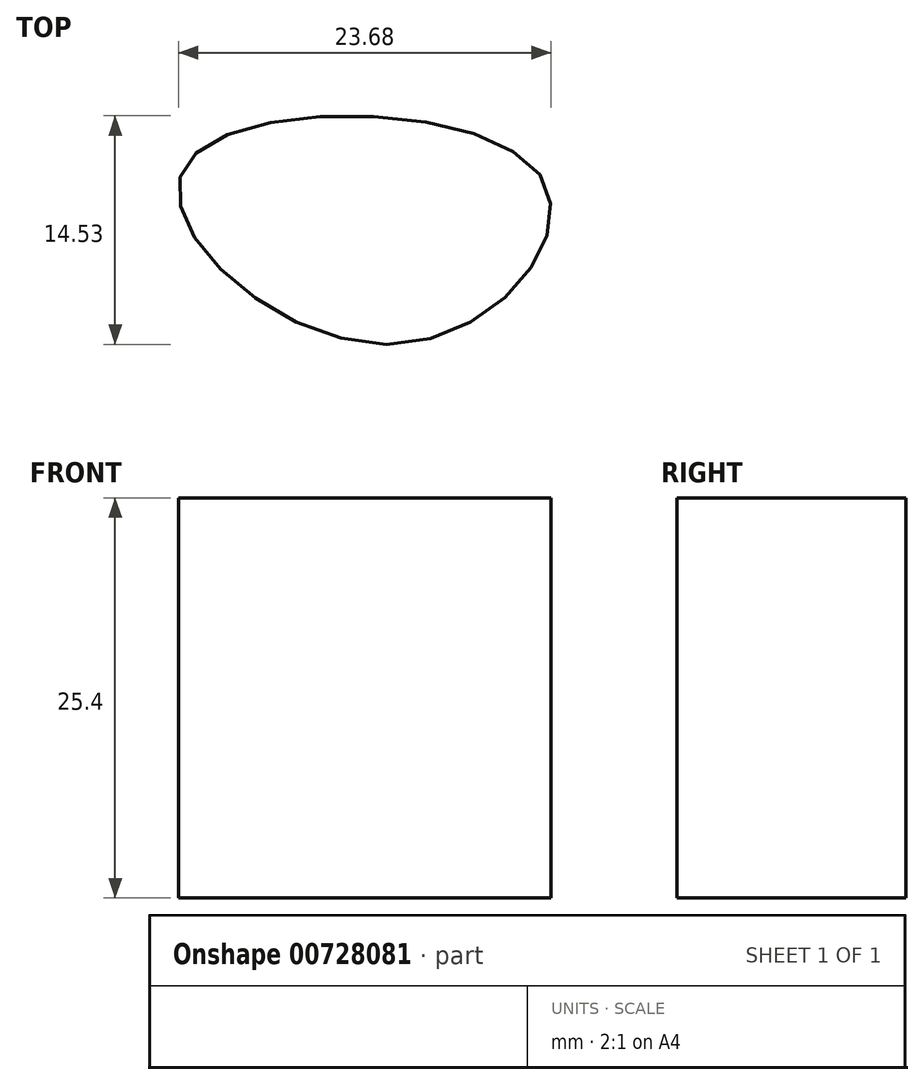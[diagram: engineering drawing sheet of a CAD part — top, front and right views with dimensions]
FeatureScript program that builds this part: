
annotation { "Feature Type Name" : "Feature", "Feature Type Description" : "" }
export const myFeature = defineFeature(function(context is Context, id is Id, definition is map)
    precondition{}
    {
        {
            var Q0;
            Q0=qCreatedBy(makeId("Top.planeOp"),FACE);
            var sketch = newSketch(context, id + "F0", { "sketchPlane" : qUnion([Q0])});
            skFitSpline(sketch, "E0", {"points": [v(-37.95, 15.13) * mm, v(24.1, 11.54) * mm, v(42.57, 38.2) * mm, v(-37.95, 15.13) * mm]});
            skSolve(sketch);
        }
        {
            var Q0;
            Q0=sQuery(id+"F0.wireOp",EDGE,"E0");
            extrude(context, id + "F1", {"bodyType" : ToolBodyType.SURFACE, "surfaceEntities" : qUnion([Q0]), "depth" : 25.4 * mm, "offsetDistance" : 25.4 * mm});
        }
        {
            var Q0;
            Q0=qCreatedBy(makeId("Top.planeOp"),FACE);
            var sketch = newSketch(context, id + "F2", { "sketchPlane" : qUnion([Q0])});
            skFitSpline(sketch, "E1", {"points": [v(22.57, 24.87) * mm, v(0, 25.39) * mm, v(13.33, 14.1) * mm, v(22.57, 24.87) * mm]});
            skSolve(sketch);
        }
        {
            var Q0;
            Q0=makeQuery(id+"F2.imprint","IMPRINT",FACE,{"disambiguationData":[TD([[makeQuery(id+"F2.imprint","IMPRINT",EDGE,{"derivedFrom":sQuery(id+"F2.wireOp",EDGE,"E1")}),1.0]])]});
            extrude(context, id + "F3", {"entities" : qUnion([Q0]), "oppositeDirection" : true, "depth" : 25.4 * mm, "offsetDistance" : 25.4 * mm});
        }
    });
